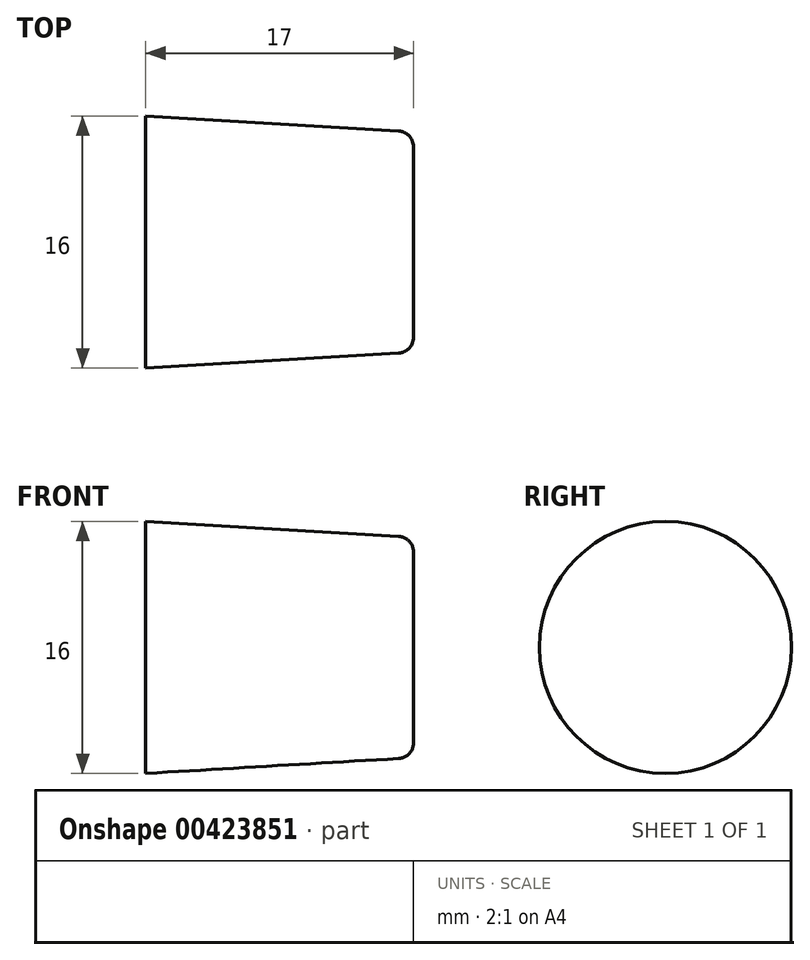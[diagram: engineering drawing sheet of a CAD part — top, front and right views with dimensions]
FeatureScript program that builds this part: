
annotation { "Feature Type Name" : "Feature", "Feature Type Description" : "" }
export const myFeature = defineFeature(function(context is Context, id is Id, definition is map)
    precondition{}
    {
        {
            var Q0;
            Q0=qCreatedBy(makeId("Front.planeOp"),FACE);
            var sketch = newSketch(context, id + "F0", { "sketchPlane" : qUnion([Q0])});
            skLineSegment(sketch, "E0", {"start": v(0, 0) * mm, "end": v(0, 8) * mm});
            skLineSegment(sketch, "E1", {"start": v(0, 8) * mm, "end": v(17, 7) * mm});
            skLineSegment(sketch, "E2", {"start": v(17, 7) * mm, "end": v(17, 0) * mm});
            skLineSegment(sketch, "E3", {"start": v(17, 0) * mm, "end": v(0, 0) * mm});
            skSolve(sketch);
        }
        {
            var Q0;
            Q0=qSketchRegion(id+"F0",true);
            var Q1;
            Q1=sQuery(id+"F0.wireOp",EDGE,"E3");
            revolve(context, id + "F1", {"entities" : qUnion([Q0]), "axis" : qUnion([Q1]), "revolveType" : RevolveType.FULL});
        }
        {
            var Q0;
            Q0=makeQuery(id+"F1.opRevolve","SWEPT_EDGE",EDGE,{"disambiguationData":[OSD([sQuery(id+"F0.wireOp",EDGE,"E1"),sQuery(id+"F0.wireOp",EDGE,"E2")])]});
            fillet(context, id + "F2", {"entities" : qUnion([Q0]), "radius" : 1 * mm, "tangentPropagation" : true, "allowEdgeOverflow" : false});
        }
    });
